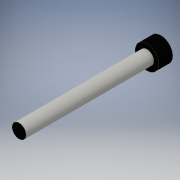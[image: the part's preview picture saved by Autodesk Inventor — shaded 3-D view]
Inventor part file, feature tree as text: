
AUTODESK INVENTOR PART (.ipt)
format: ipt  version: 2016 (Build 200138000, 138)  size: 98,816 bytes
history: native  units: in
note: dims shown in document units (in); Inventor stores cm internally (conversion verified against a paired STEP export)
features: extrude x2, sketch x2
ambient origin geometry x8: Origin, YZ Plane, XZ Plane, XY Plane, X Axis, Y Axis, Z Axis, Center Point
bodies: Solid1 (feature_tree)
feature tree (4):
  extrude  "Extrusion1"  Depth=0.1969in TaperAngle=0.0deg
  extrude  "Extrusion2"  Depth=1.811in TaperAngle=0.0deg
  sketch  "Sketch1"  dims[d0=0.3346in d1=0.1969in d2=0.0in]
  sketch  "Sketch2"  dims[d3=0.1969in d4=1.811in d5=0.0in]
